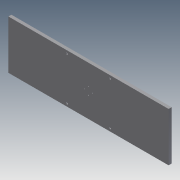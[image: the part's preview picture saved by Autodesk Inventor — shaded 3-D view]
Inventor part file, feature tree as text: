
AUTODESK INVENTOR PART (.ipt)
format: ipt  version: 2011 (Build 150239000, 239)  size: 99,328 bytes
history: native  units: in
note: dims shown in document units (in); Inventor stores cm internally (conversion verified against a paired STEP export)
features: extrude x3, sketch x3
ambient origin geometry x8: Origin, YZ Plane, XZ Plane, XY Plane, X Axis, Y Axis, Z Axis, Center Point
bodies: Solid1 (feature_tree)
feature tree (6):
  extrude  "Extrusion1"  Depth=4.0in
  extrude  "Extrusion2"  Depth=0.6299in
  extrude  "Extrusion3"  Depth=0.0787in
  sketch  "Sketch1"  dims[d0=13.14in d1=4.0in]
  sketch  "Sketch2"  dims[d2=0.25in d3=0.0in d4=0.6299in]
  sketch  "Sketch3"  dims[d5=0.0787in d6=0.0787in d7=0.0787in d8=0.0787in d9=0.25in d10=0.0in d11=1.765in d12=1.765in d13=3.53in d14=3.53in d15=0.156in d16=0.156in d17=0.156in d18=0.25in d19=0.0in]
